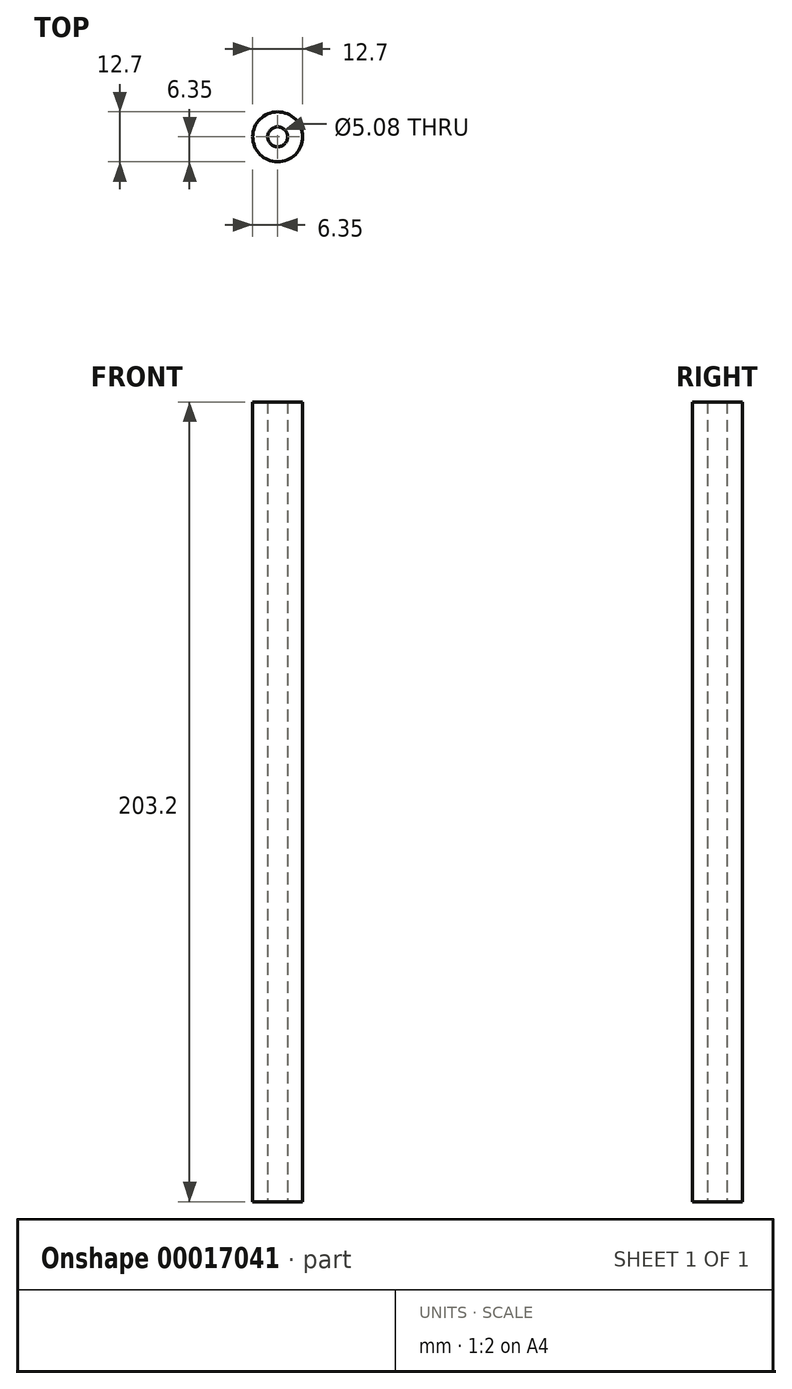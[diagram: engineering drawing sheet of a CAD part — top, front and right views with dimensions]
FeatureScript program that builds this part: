
annotation { "Feature Type Name" : "Feature", "Feature Type Description" : "" }
export const myFeature = defineFeature(function(context is Context, id is Id, definition is map)
    precondition{}
    {
        {
            var Q0;
            Q0=qCreatedBy(makeId("Top.planeOp"),FACE);
            var sketch = newSketch(context, id + "F0", { "sketchPlane" : qUnion([Q0])});
            skCircle(sketch, "E0", {"center": v(0, 0) * mm, "radius": 6.35 * mm});
            skCircle(sketch, "E1", {"center": v(0, 0) * mm, "radius": 2.54 * mm});
            skSolve(sketch);
        }
        {
            var Q0;
            Q0 = qSketchRegion(id + "F0", true);
            extrude(context, id + "F1", {"entities" : qUnion([Q0]), "depth" : 203.2 * mm});
        }
    });
